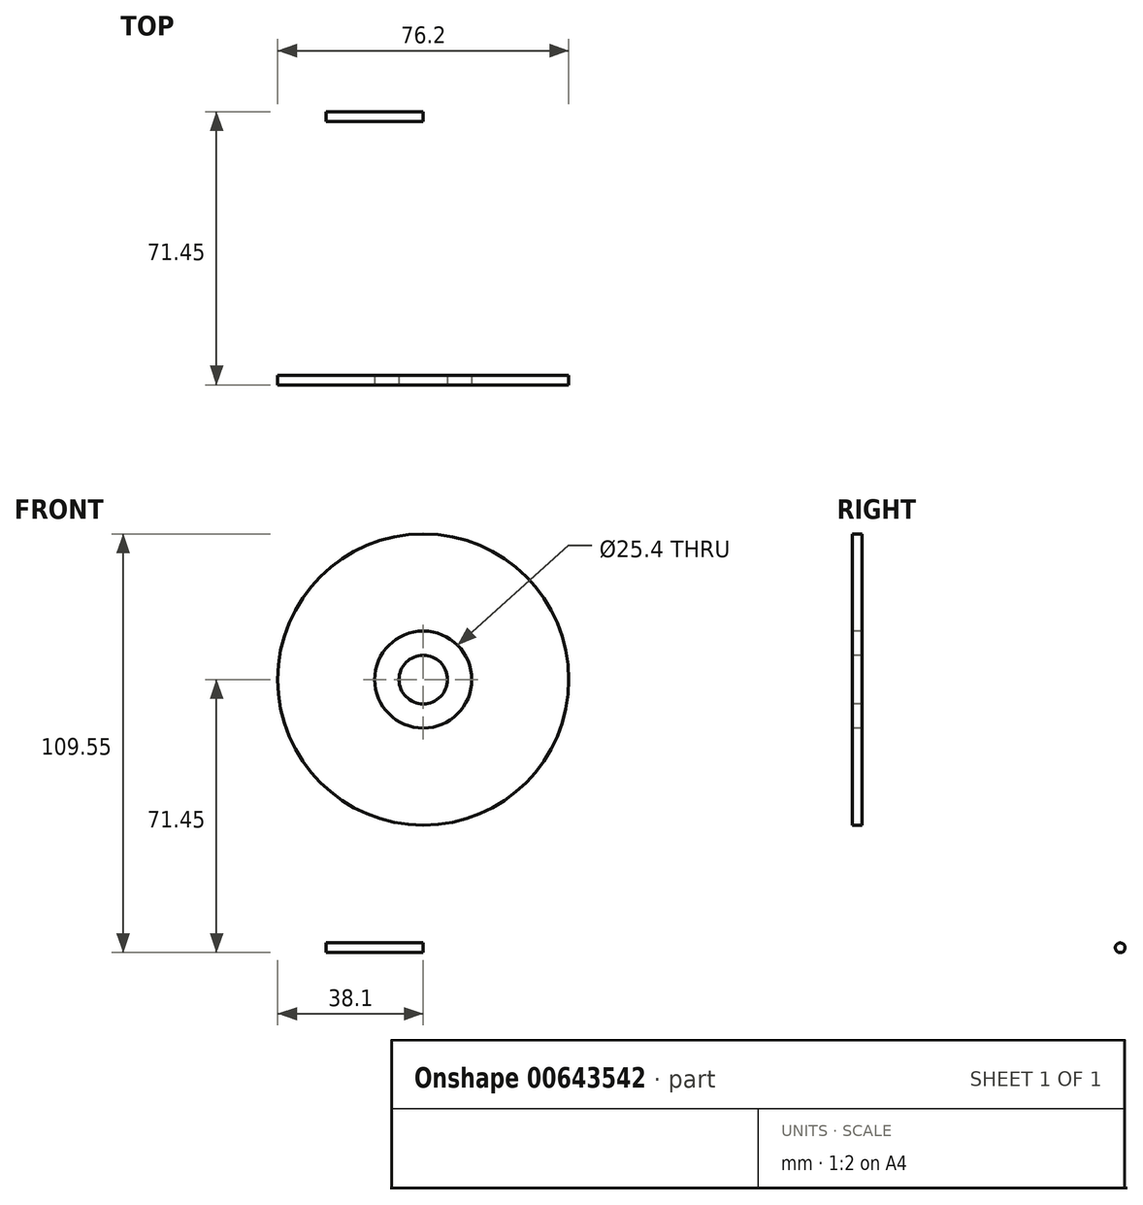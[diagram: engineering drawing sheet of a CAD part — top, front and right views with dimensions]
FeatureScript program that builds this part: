
annotation { "Feature Type Name" : "Feature", "Feature Type Description" : "" }
export const myFeature = defineFeature(function(context is Context, id is Id, definition is map)
    precondition{}
    {
        {
            var Q0;
            Q0=qCreatedBy(makeId("Front.planeOp"),FACE);
            var sketch = newSketch(context, id + "F0", { "sketchPlane" : qUnion([Q0])});
            skCircle(sketch, "E0", {"center": v(0, 0) * mm, "radius": 12.7 * mm});
            skCircle(sketch, "E1", {"center": v(0, 0) * mm, "radius": 6.35 * mm});
            skCircle(sketch, "E2", {"center": v(0, 0) * mm, "radius": 38.1 * mm});
            skSolve(sketch);
        }
        {
            var Q0;
            Q0=makeQuery(id+"F0.imprint","IMPRINT",FACE,{"disambiguationData":[TD([[makeQuery(id+"F0.imprint","IMPRINT",EDGE,{"derivedFrom":sQuery(id+"F0.wireOp",EDGE,"E0")}),-1.0]])]});
            var Q1;
            Q1=makeQuery(id+"F0.imprint","IMPRINT",FACE,{"disambiguationData":[TD([[makeQuery(id+"F0.imprint","IMPRINT",EDGE,{"derivedFrom":sQuery(id+"F0.wireOp",EDGE,"E1")}),1.0]])]});
            extrude(context, id + "F1", {"entities" : qUnion([Q0, Q1]), "oppositeDirection" : true, "depth" : 2.54 * mm, "offsetDistance" : 25.4 * mm});
        }
        {
            var Q0;
            Q0=qCreatedBy(makeId("Right.planeOp"),FACE);
            var sketch = newSketch(context, id + "F2", { "sketchPlane" : qUnion([Q0])});
            skCircle(sketch, "E3", {"center": v(70.18, -70.18) * mm, "radius": 1.27 * mm});
            skSolve(sketch);
        }
        {
            var Q0;
            Q0=makeQuery(id+"F2.imprint","IMPRINT",FACE,{"disambiguationData":[TD([[makeQuery(id+"F2.imprint","IMPRINT",EDGE,{"derivedFrom":sQuery(id+"F2.wireOp",EDGE,"E3")}),1.0]])]});
            extrude(context, id + "F3", {"entities" : qUnion([Q0]), "oppositeDirection" : true, "depth" : 25.4 * mm, "offsetDistance" : 25.4 * mm});
        }
    });
